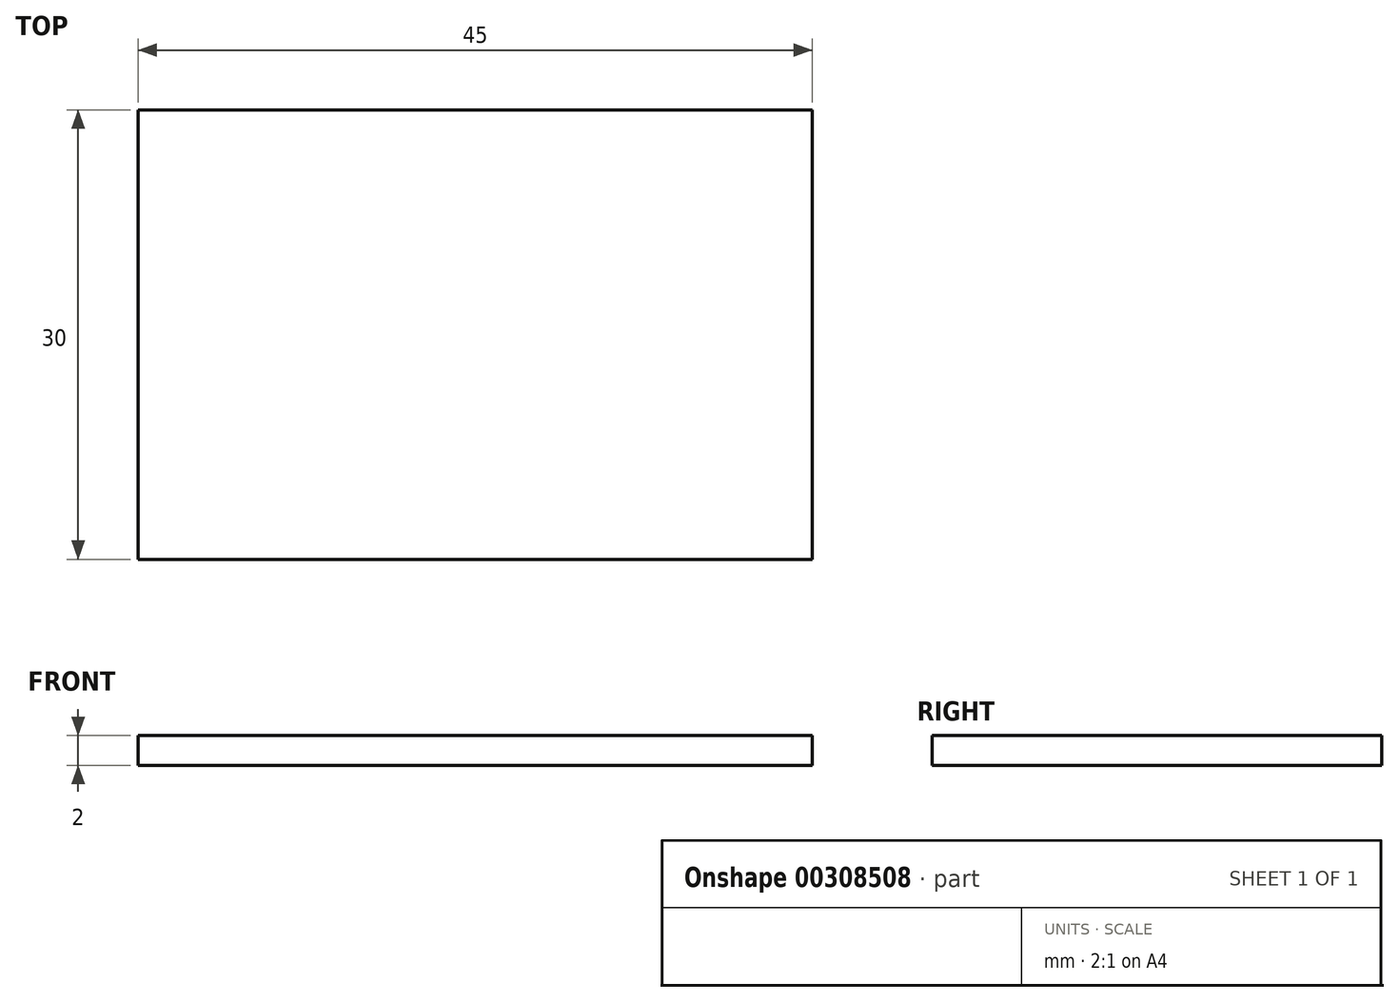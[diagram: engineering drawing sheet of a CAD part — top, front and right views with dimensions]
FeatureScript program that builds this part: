
annotation { "Feature Type Name" : "Feature", "Feature Type Description" : "" }
export const myFeature = defineFeature(function(context is Context, id is Id, definition is map)
    precondition{}
    {
        {
            var Q0;
            Q0=qCreatedBy(makeId("Top.planeOp"),FACE);
            var sketch = newSketch(context, id + "F0", { "sketchPlane" : qUnion([Q0])});
            skLineSegment(sketch, "E0.bottom", {"start": v(-35.62, 69.67) * mm, "end": v(9.38, 69.67) * mm});
            skLineSegment(sketch, "E0.top", {"start": v(-35.62, 39.67) * mm, "end": v(9.38, 39.67) * mm});
            skLineSegment(sketch, "E0.left", {"start": v(-35.62, 69.67) * mm, "end": v(-35.62, 39.67) * mm});
            skLineSegment(sketch, "E0.right", {"start": v(9.38, 69.67) * mm, "end": v(9.38, 39.67) * mm});
            skSolve(sketch);
        }
        {
            var Q0;
            Q0 = qSketchRegion(id + "F0", true);
            extrude(context, id + "F1", {"entities" : qUnion([Q0]), "depth" : 2 * mm});
        }
    });
